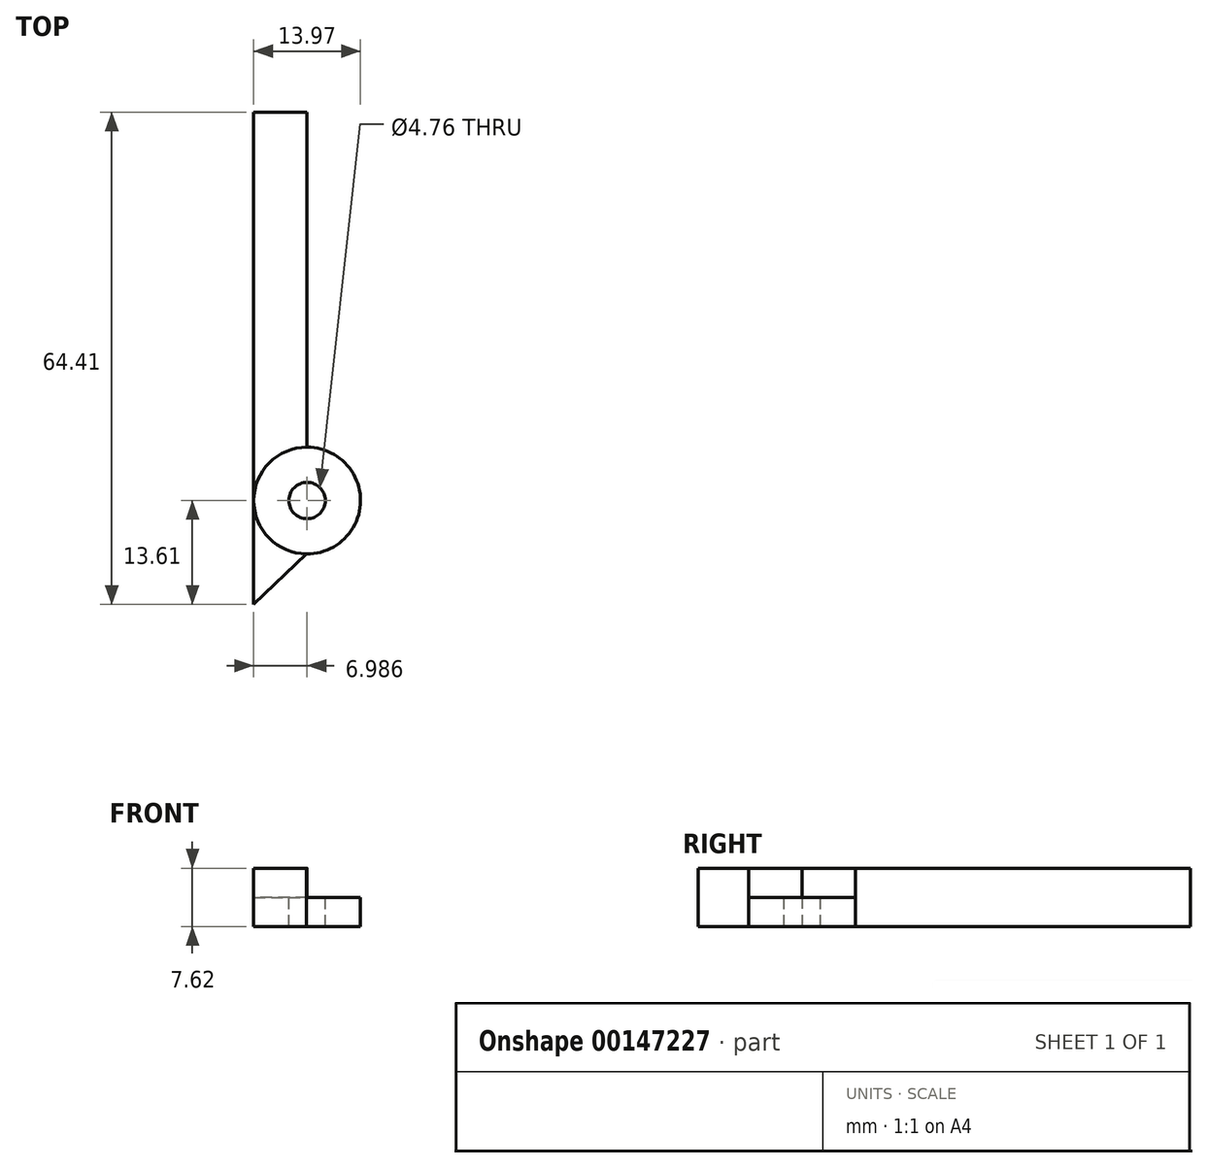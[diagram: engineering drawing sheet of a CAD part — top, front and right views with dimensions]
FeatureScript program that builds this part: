
annotation { "Feature Type Name" : "Feature", "Feature Type Description" : "" }
export const myFeature = defineFeature(function(context is Context, id is Id, definition is map)
    precondition{}
    {
        {
            var Q0;
            Q0=qCreatedBy(makeId("Top.planeOp"),FACE);
            var sketch = newSketch(context, id + "F0", { "sketchPlane" : qUnion([Q0])});
            skLineSegment(sketch, "E0.bottom", {"start": v(4.37, -25.4) * mm, "end": v(-2.62, -25.4) * mm});
            skLineSegment(sketch, "E0.top", {"start": v(4.37, 25.4) * mm, "end": v(-2.62, 25.4) * mm});
            skLineSegment(sketch, "E0.left", {"start": v(4.37, -25.4) * mm, "end": v(4.37, 25.4) * mm});
            skLineSegment(sketch, "E0.right", {"start": v(-2.62, -25.4) * mm, "end": v(-2.62, 25.4) * mm});
            skPoint(sketch, "E0.middle", {"position": v(0.87, 0) * mm});
            skCircle(sketch, "E1", {"center": v(4.37, -25.4) * mm, "radius": 6.99 * mm});
            skSolve(sketch);
        }
        {
            var Q0;
            {var subQ0=sQuery(id+"F0.wireOp",EDGE,"E0.top");Q0=makeQuery(id+"F0.imprint","IMPRINT",FACE,{"disambiguationData":[TD([[makeQuery(id+"F0.imprint","IMPRINT",EDGE,{"derivedFrom":subQ0}),1.0]])]});}
            var Q1;
            {var subQ0=sQuery(id+"F0.wireOp",EDGE,"E0.bottom");Q1=makeQuery(id+"F0.imprint","IMPRINT",FACE,{"disambiguationData":[TD([[makeQuery(id+"F0.imprint","IMPRINT",EDGE,{"derivedFrom":subQ0}),1.0]])]});}
            var Q2;
            {var subQ0=sQuery(id+"F0.wireOp",EDGE,"E0.bottom");Q2=makeQuery(id+"F0.imprint","IMPRINT",FACE,{"disambiguationData":[TD([[makeQuery(id+"F0.imprint","IMPRINT",EDGE,{"derivedFrom":subQ0}),-1.0]])]});}
            extrude(context, id + "F1", {"entities" : qUnion([Q0, Q1, Q2]), "oppositeDirection" : true, "depth" : 7.62 * mm});
        }
        {
            var Q0;
            Q0=makeQuery(id+"F1.opExtrude","CAP_FACE",FACE,{"disambiguationData":[OSD([sQuery(id+"F0.wireOp",EDGE,"E0.top"),sQuery(id+"F0.wireOp",EDGE,"E0.left"),sQuery(id+"F0.wireOp",EDGE,"E0.right"),sQuery(id+"F0.wireOp",EDGE,"E1")])],"isStart":true});
            var sketch = newSketch(context, id + "F2", { "sketchPlane" : qUnion([Q0])});
            skCircle(sketch, "E2", {"center": v(4.37, -25.4) * mm, "radius": 6.99 * mm});
            skSolve(sketch);
        }
        {
            var Q0;
            {var subQ0=sQuery(id+"F2.wireOp",EDGE,"E2");var subQ1=makeQuery(id+"F2.imprint","INTERSECT",VERTEX,{"derivedFrom":[makeQuery(id+"F1.opExtrude","CAP_EDGE",EDGE,{"disambiguationData":[OSD([sQuery(id+"F0.wireOp",EDGE,"E0.right")])],"isStart":true}),subQ0]});Q0=makeQuery(id+"F2.imprint","IMPRINT",FACE,{"disambiguationData":[TD([[makeQuery(id+"F2.imprint","IMPRINT",EDGE,{"disambiguationData":[TD([[subQ1,1.0]])],"derivedFrom":subQ0}),1.0]])]});}
            extrude(context, id + "F3", {"entities" : qUnion([Q0]), "operationType" : NewBodyOperationType.REMOVE, "oppositeDirection" : true, "depth" : 3.8 * mm});
        }
        {
            var Q0;
            Q0=makeQuery(id+"F3.boolean.opBoolean","COPY",FACE,{"derivedFrom":makeQuery(id+"F3.opExtrude","CAP_FACE",FACE,{"disambiguationData":[OSD([sQuery(id+"F2.wireOp",EDGE,"E2")])],"isStart":false})});
            var sketch = newSketch(context, id + "F4", { "sketchPlane" : qUnion([Q0])});
            skPoint(sketch, "E3", {"position": v(4.37, -25.4) * mm});
            skSolve(sketch);
        }
        {
            var Q0;
            Q0=sQuery(id+"F4.wireOp",VERTEX,"E3");
            var Q1;
            Q1=makeQuery(id+"F1.opExtrude","SWEPT_BODY",BODY,{"disambiguationData":[OSD([sQuery(id+"F0.wireOp",EDGE,"E0.top"),sQuery(id+"F0.wireOp",EDGE,"E0.left"),sQuery(id+"F0.wireOp",EDGE,"E0.right"),sQuery(id+"F0.wireOp",EDGE,"E1")])]});
            hole(context, id + "F5", {"style" : HoleStyle.SIMPLE, "endStyle" : HoleEndStyle.BLIND, "holeDiameter" : 4.76 * mm, "holeDepth" : 12.7 * mm, "locations" : qUnion([Q0]), "scope" : qUnion([Q1])});
        }
        {
            var Q0;
            Q0=makeQuery(id+"F1.opExtrude","CAP_FACE",FACE,{"disambiguationData":[OSD([sQuery(id+"F0.wireOp",EDGE,"E0.top"),sQuery(id+"F0.wireOp",EDGE,"E0.left"),sQuery(id+"F0.wireOp",EDGE,"E0.right"),sQuery(id+"F0.wireOp",EDGE,"E1")])],"isStart":false});
            var sketch = newSketch(context, id + "F6", { "sketchPlane" : qUnion([Q0])});
            skLineSegment(sketch, "E4", {"start": v(-2.62, 25.4) * mm, "end": v(-2.62, 39.01) * mm});
            skLineSegment(sketch, "E5", {"start": v(-2.62, 39.01) * mm, "end": v(4.3, 32.38) * mm});
            skSolve(sketch);
        }
        {
            var Q0;
            {var subQ0=sQuery(id+"F6.wireOp",EDGE,"E4");Q0=makeQuery(id+"F6.imprint","IMPRINT",FACE,{"disambiguationData":[TD([[makeQuery(id+"F6.imprint","IMPRINT",EDGE,{"derivedFrom":subQ0}),-1.0]])]});}
            extrude(context, id + "F7", {"entities" : qUnion([Q0]), "oppositeDirection" : true, "depth" : 7.62 * mm});
        }
    });
